# Revit family: Hager-Volta-IP30-Flush_mounted-syst-NoHosted-PL-en
name_source: partatom
category: Electrical Equipment
units: mm (PartAtom-declared; Revit-internal decimal feet)

## family parameters
Always vertical = Yes
Cut with Voids When Loaded = No
Panel Configuration = Two Columns, Circuits Across
Part Type = Panelboard
Room Calculation Point = No
Round Connector Dimension = Use Diameter
Shared = No
Work Plane-Based = Yes

## types (17) — shared parameters
Default Elevation = 1219 mm
EF000003 - Mounting method = EV000383 - Flush mounted (plaster)
EF000008 - Width = 348 mm  [stored 1.14173 ft]
EF000116 - RAL-number = 9010
EF000218 - Built-in depth = 89 mm  [stored 0.291995 ft]
EF000846 - Built-in width = 314 mm  [stored 1.03018 ft]
EF001062 - EMC-version = No
EF002950 - Width in number of modular spacings = 12
EF004462 - Type of closure = EV000154 - Other
EF005474 - Degree of protection (IP) = EV006410 - IP30
EF006244 - Transparent cover/door = No
EF006306 - With lock = No
EF015941 - Signal passing door = No
HG000001 - Number of columns = 1
HG000003 - Range = Volta
HG000005 - Thickness = 3 mm  [stored 0.00984252 ft]
HG000006 - Flush mounted = Yes
HG000009 - Double swing door = No
HG000010 - Asymmetric doors = No
HG000017 - Distance between poles = 18 mm  [stored 0.0590551 ft]
Manufacturer = Hager
Type Comments = Volta
zero-valued in all types: HG000007 - Number of empty columns

## per-type parameters (varying)
| type | EF000007 - Colour | EF000040 - Height | EF000049 - Depth | EF000118 - With mounting plate | EF000266 - Number of rows | EF000332 - Built-in height | EF000339 - Type of cover | EF001088 - Extension possible | EF001131 - Internal depth | EF001134 - DIN-rail | EF001596 - Material housing | EF009212 - Cover model | EF015776 - Earthing terminal block | EF015777 - Neutral terminal block | HG000002 - With door or cover | HG000004 - Manufacturer reference | HG000008 - Number of empty rows | HG000011 - Empty rows from bottom | Model |
| Recessed mounted IP30 W348 H356.5 D98 12 Modular spacings - VU12AT | EV000202 - White | 356 mm  [stored 1.16798 ft] | 98 mm  [stored 0.321522 ft] | No | 1 | 321 mm  [stored 1.05315 ft] | EV004216 - Door | Yes | 92 mm  [stored 0.301837 ft] | Yes | EV000139 - Plastic | EV009916 - With notch | Yes | Yes | Yes | VU12AT | 0 | No | VU12AT |
| Recessed mounted IP30 W348 H356.5 D98 12 Modular spacings - VU12NE | EV000202 - White | 356 mm  [stored 1.16798 ft] | 98 mm  [stored 0.321522 ft] | No | 1 | 321 mm  [stored 1.05315 ft] | EV004216 - Door | Yes | 92 mm  [stored 0.301837 ft] | Yes | EV000139 - Plastic | EV009916 - With notch | Yes | No | Yes | VU12NE | 0 | No | VU12NE |
| Recessed mounted IP30 W348 H505.5 D98 12 Modular spacings - VU24AT | EV000202 - White | 506 mm  [stored 1.6601 ft] | 98 mm  [stored 0.321522 ft] | No | 2 | 470 mm  [stored 1.54199 ft] | EV004216 - Door | Yes | 92 mm  [stored 0.301837 ft] | Yes | EV000139 - Plastic | EV009916 - With notch | Yes | Yes | Yes | VU24AT | 0 | No | VU24AT |
| Recessed mounted IP30 W348 H505.5 D98 12 Modular spacings - VU24NE | EV000202 - White | 506 mm  [stored 1.6601 ft] | 98 mm  [stored 0.321522 ft] | No | 2 | 470 mm  [stored 1.54199 ft] | EV004216 - Door | Yes | 92 mm  [stored 0.301837 ft] | Yes | EV000139 - Plastic | EV009916 - With notch | Yes | No | Yes | VU24NE | 0 | No | VU24NE |
| Recessed mounted IP30 W348 H630.5 D98 12 Modular spacings - VU36AT | EV000202 - White | 630 mm  [stored 2.06693 ft] | 98 mm  [stored 0.321522 ft] | No | 3 | 595 mm  [stored 1.9521 ft] | EV004216 - Door | Yes | 92 mm  [stored 0.301837 ft] | Yes | EV000139 - Plastic | EV009916 - With notch | Yes | Yes | Yes | VU36AT | 0 | No | VU36AT |
| Recessed mounted IP30 W348 H630.5 D98 12 Modular spacings - VU36NE | EV000202 - White | 630 mm  [stored 2.06693 ft] | 98 mm  [stored 0.321522 ft] | No | 3 | 595 mm  [stored 1.9521 ft] | EV004216 - Door | Yes | 92 mm  [stored 0.301837 ft] | Yes | EV000139 - Plastic | EV009916 - With notch | Yes | No | Yes | VU36NE | 0 | No | VU36NE |
| Recessed mounted IP30 W348 H630.5 D98 12 Modular spacings - VU36NE-MBN | EV000202 - White | 630 mm  [stored 2.06693 ft] | 98 mm  [stored 0.321522 ft] | No | 3 | 595 mm  [stored 1.9521 ft] | EV004216 - Door | Yes | 92 mm  [stored 0.301837 ft] | Yes | EV000139 - Plastic | EV009916 - With notch | Yes | No | Yes | VU36NE-MBN | 0 | No | VU36NE-MBN |
| Recessed mounted IP30 W348 H755.5 D98 12 Modular spacings - VU48AT | EV000202 - White | 756 mm  [stored 2.48031 ft] | 98 mm  [stored 0.321522 ft] | No | 4 | 720 mm  [stored 2.3622 ft] | EV004216 - Door | Yes | 92 mm  [stored 0.301837 ft] | Yes | EV000139 - Plastic | EV009916 - With notch | Yes | Yes | Yes | VU48AT | 0 | No | VU48AT |
| Recessed mounted IP30 W348 H755.5 D98 12 Modular spacings - VU48NE | EV000202 - White | 756 mm  [stored 2.48031 ft] | 98 mm  [stored 0.321522 ft] | No | 4 | 720 mm  [stored 2.3622 ft] | EV004216 - Door | Yes | 92 mm  [stored 0.301837 ft] | Yes | EV000139 - Plastic | EV009916 - With notch | Yes | No | Yes | VU48NE | 0 | No | VU48NE |
| Recessed mounted IP30 W348 H755.5 D98 12 Modular spacings - VU48NJ |  | 756 mm  [stored 2.48031 ft] | 98 mm  [stored 0.321522 ft] | No | 4 | 720 mm  [stored 2.3622 ft] |  | No | 0 mm  [stored 0 ft] | No | EV000154 - Other |  | Yes | No | No | VU48NJ | 0 | No | VU48NJ |
| Recessed mounted IP30 W348 H880.5 D94.5 12 Modular spacings - VU60NC | EV000202 - White | 880 mm  [stored 2.88714 ft] | 94 mm  [stored 0.308399 ft] | No | 5 | 845 mm  [stored 2.77231 ft] | EV004216 - Door | Yes | 92 mm  [stored 0.301837 ft] | Yes | EV000139 - Plastic | EV009916 - With notch | No | No | Yes | VU60NC | 0 | No | VU60NC |
| Recessed mounted IP30 W348 H880.5 D98 12 Modular spacings - VU601PLH | EV000202 - White | 880 mm  [stored 2.88714 ft] | 98 mm  [stored 0.321522 ft] | Yes | 1 | 845 mm  [stored 2.77231 ft] | EV004216 - Door | Yes | 92 mm  [stored 0.301837 ft] | Yes | EV000154 - Other | EV009916 - With notch | Yes | Yes | Yes | VU601PLH | 4 | Yes | VU601PLH |
| Recessed mounted IP30 W348 H880.5 D98 12 Modular spacings - VU602PLH | EV000202 - White | 880 mm  [stored 2.88714 ft] | 98 mm  [stored 0.321522 ft] | Yes | 2 | 845 mm  [stored 2.77231 ft] | EV004216 - Door | Yes | 92 mm  [stored 0.301837 ft] | Yes | EV000154 - Other | EV009916 - With notch | Yes | Yes | Yes | VU602PLH | 3 | Yes | VU602PLH |
| Recessed mounted IP30 W348 H880.5 D98 12 Modular spacings - VU603PLG | EV000202 - White | 880 mm  [stored 2.88714 ft] | 98 mm  [stored 0.321522 ft] | Yes | 3 | 845 mm  [stored 2.77231 ft] | EV004216 - Door | Yes | 92 mm  [stored 0.301837 ft] | Yes | EV000154 - Other | EV009916 - With notch | Yes | No | Yes | VU603PLG | 2 | Yes | VU603PLG |
| Recessed mounted IP30 W348 H880.5 D98 12 Modular spacings - VU603PLH | EV000202 - White | 880 mm  [stored 2.88714 ft] | 98 mm  [stored 0.321522 ft] | Yes | 3 | 845 mm  [stored 2.77231 ft] | EV004216 - Door | Yes | 92 mm  [stored 0.301837 ft] | Yes | EV000154 - Other | EV009916 - With notch | Yes | Yes | Yes | VU603PLH | 2 | Yes | VU603PLH |
| Recessed mounted IP30 W348 H880.5 D98 12 Modular spacings - VU60AT | EV000202 - White | 880 mm  [stored 2.88714 ft] | 98 mm  [stored 0.321522 ft] | No | 5 | 845 mm  [stored 2.77231 ft] | EV004216 - Door | Yes | 92 mm  [stored 0.301837 ft] | Yes | EV000139 - Plastic | EV009916 - With notch | Yes | No | Yes | VU60AT | 0 | No | VU60AT |
| Recessed mounted IP30 W348 H880.5 D98 12 Modular spacings - VU60NC-MBN | EV000202 - White | 880 mm  [stored 2.88714 ft] | 98 mm  [stored 0.321522 ft] | No | 5 | 845 mm  [stored 2.77231 ft] | EV004216 - Door | Yes | 92 mm  [stored 0.301837 ft] | Yes | EV000139 - Plastic | EV009916 - With notch | Yes | No | Yes | VU60NC-MBN | 0 | No | VU60NC-MBN |

note: [stored X ft] marks values corroborated as IEEE doubles in the binary element streams (Revit-internal decimal feet)

## geometry (parser evidence)
native form markers: Sweep x14
no freeform markers — native parametric forms only
